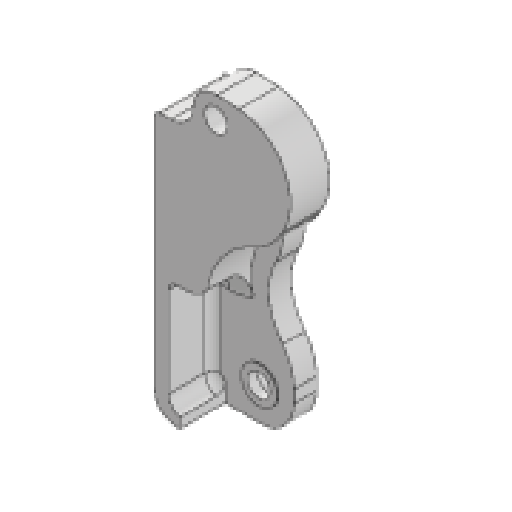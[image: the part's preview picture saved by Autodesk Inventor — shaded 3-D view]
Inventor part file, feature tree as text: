
AUTODESK INVENTOR PART (.ipt)
format: ipt  version: 2025 (Build 290162000, 162)  size: 379,392 bytes
history: native  units: mm
features: extrude x14, sketch x14, fillet x13, projected_geometry x13, other x5, reference x3, thicken_offset x1
ambient origin geometry x8: Origin, YZ Plane, XZ Plane, XY Plane, X Axis, Y Axis, Z Axis, Center Point
bodies: Solid1 (feature_tree)
feature tree (63):
  extrude  "Extrusion1"  Depth=8.0mm
  extrude  "Extrusion2"  Depth=10.0mm
  extrude  "Extrusion3"  Depth=10.0mm TaperAngle=0.0deg
  extrude  "Extrusion4"  Depth=10.0mm TaperAngle=0.0deg
  fillet  "Fillet1"  Radius=20.0mm
  extrude  "Extrusion5"  Depth=5.0mm
  fillet  "Fillet2"  Radius=5.0mm
  extrude  "Extrusion6"  Depth=10.0mm TaperAngle=0.0deg
  extrude  "Extrusion7"  Depth=10.0mm TaperAngle=0.0deg
  extrude  "Extrusion8"  Depth=0.5mm TaperAngle=0.0deg
  extrude  "Extrusion9"  Depth=5.0mm
  extrude  "Extrusion10"  Depth=8.0mm
  extrude  "Extrusion11"  Depth=20.0mm
  extrude  "Extrusion12"  Depth=5.0mm
  thicken_offset  "Thicken1"
  fillet  "Fillet4"  Radius=8.0mm
  fillet  "Fillet5"  Radius=3.0mm
  fillet  "Fillet6"  Radius=20.0mm
  extrude  "Extrusion13"  Depth=2.0mm
  fillet  "Fillet7"  Radius=20.0mm
  extrude  "Extrusion14"  [1 undecoded]
  fillet  "Fillet8"  [1 undecoded]
  fillet  "Fillet9"  [1 undecoded]
  fillet  "Fillet10"  [1 undecoded]
  fillet  "Fillet11"  [1 undecoded]
  fillet  "Fillet13"  [1 undecoded]
  fillet  "Fillet14"  [1 undecoded]
  fillet  "Fillet15"  [1 undecoded]
  sketch  "Sketch1"  dims[d0=90.0mm d1=8.0mm]
  reference  "Reference1"
  sketch  "Sketch2"  dims[d2=10.0mm d3=0.0mm d4=8.2mm]
  projected_geometry  "Projected Loop1"
  sketch  "Sketch3"  dims[d5=8.2mm d6=10.0mm d7=0.0mm]
  projected_geometry  "Projected Loop2"
  sketch  "Sketch4"  dims[d8=12.0mm d9=0.0mm d10=10.0mm d11=0.0mm d12=20.0mm]
  projected_geometry  "Projected Loop3"
  sketch  "Sketch5"  dims[d13=10.0mm d14=0.0mm d15=4.0mm d16=5.0mm d17=0.0mm]
  projected_geometry  "Projected Loop4"
  sketch  "Sketch6"  dims[d18=10.0mm d19=0.0mm d20=10.0mm d21=0.0mm]
  sketch  "Sketch7"  dims[d22=0.0mm d23=0.0mm d24=10.0mm d25=0.0mm]
  projected_geometry  "Projected Loop5"
  projected_geometry  "Projected Loop6"
  reference  "Reference2"
  reference  "Reference3"
  sketch  "Sketch8"  dims[d27=0.5mm d28=0.0mm d29=0.5mm d30=0.0mm]
  projected_geometry  "Projected Loop7"
  sketch  "Sketch9"  dims[d31=4.0mm d32=5.0mm d33=6.0mm]
  projected_geometry  "Projected Loop8"
  sketch  "Sketch10"  dims[d34=10.0mm d35=8.0mm]
  projected_geometry  "Projected Loop9"
  sketch  "Sketch11"  dims[d36=5.0mm d37=0.0mm d38=20.0mm]
  projected_geometry  "Projected Loop10"
  sketch  "Sketch12"  dims[d39=5.0mm d40=0.0mm d41=5.0mm d42=8.0mm d43=3.0mm d44=20.0mm]
  projected_geometry  "Projected Loop11"
  sketch  "Sketch13"  dims[d46=8.0mm d47=2.0mm d48=20.0mm]
  projected_geometry  "Projected Loop12"
  sketch  "Sketch14"
  projected_geometry  "Projected Loop13"
  other  "<userpath>\Desktop\puppycat\rearSwingarm.iam"
  other  "rearSwingarm.iam"
  other  "rearSwingarmBaseV1:1"
  other  "6082rsBearing:14"
  other  "b link:2"
note: 8 required parameter values undecoded (feature->parameter linkage not recoverable at this tier; creation-order binding heuristic only, values carry confidence <= 0.55)
